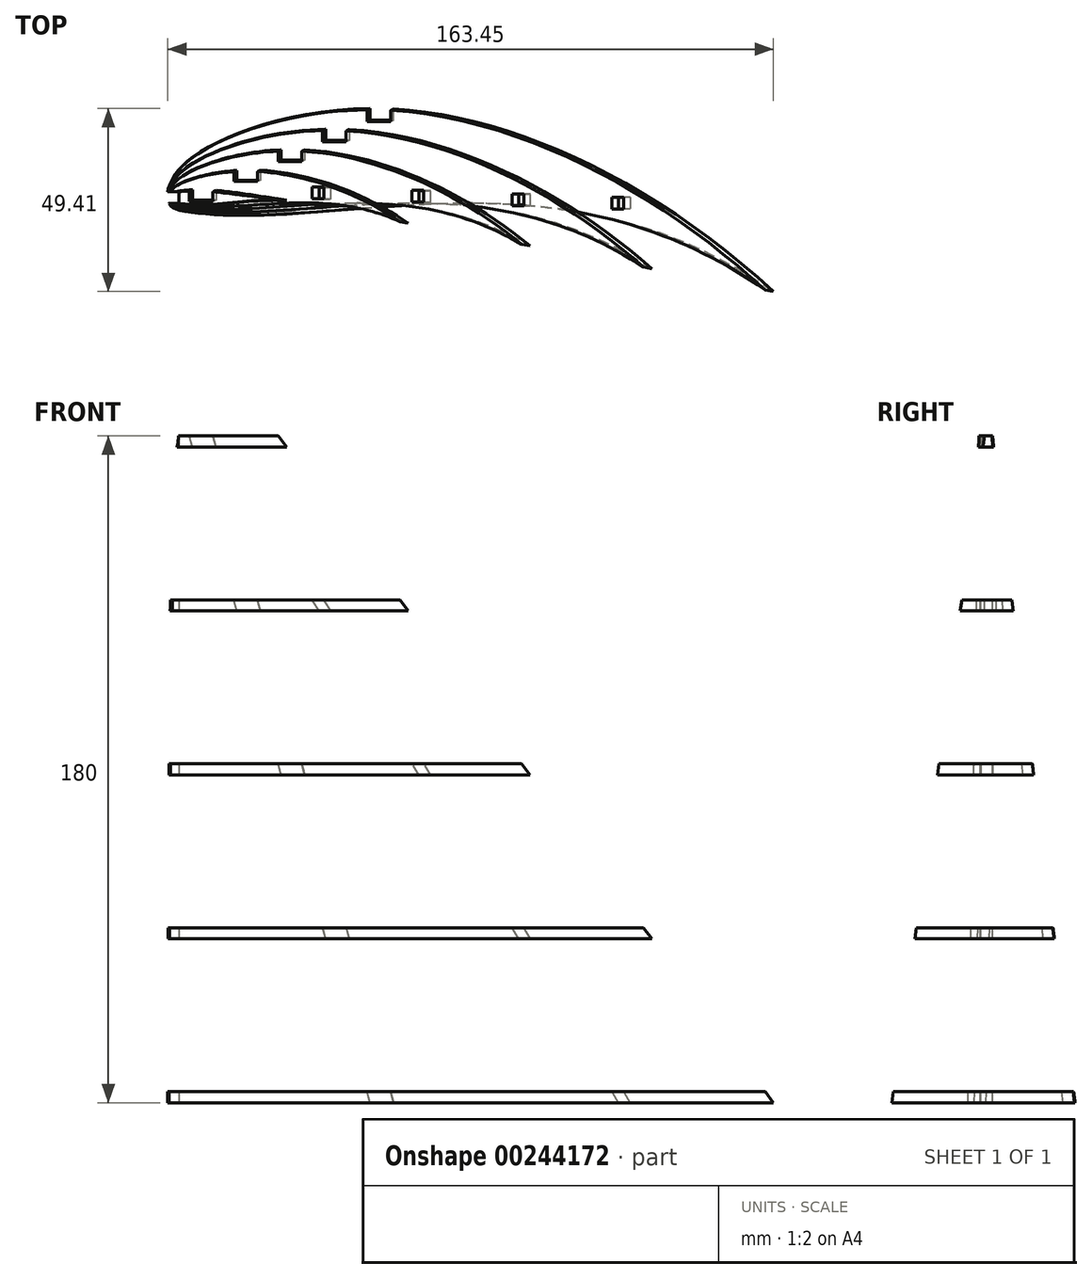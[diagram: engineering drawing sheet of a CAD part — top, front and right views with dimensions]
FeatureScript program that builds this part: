
annotation { "Feature Type Name" : "Feature", "Feature Type Description" : "" }
export const myFeature = defineFeature(function(context is Context, id is Id, definition is map)
    precondition{}
    {
        {
            var Q0;
            Q0=qCreatedBy(makeId("Top.planeOp"),FACE);
            var sketch = newSketch(context, id + "F0", { "sketchPlane" : qUnion([Q0])});
            skLineSegment(sketch, "E0", {"start": v(1.56, 5.68) * mm, "end": v(5.56, 9.57) * mm});
            skLineSegment(sketch, "E1", {"start": v(5.56, 9.57) * mm, "end": v(7.64, 11.4) * mm});
            skLineSegment(sketch, "E2", {"start": v(7.64, 11.4) * mm, "end": v(10.4, 13.54) * mm});
            skLineSegment(sketch, "E3", {"start": v(10.4, 13.54) * mm, "end": v(12.1, 14.65) * mm});
            skLineSegment(sketch, "E4", {"start": v(12.1, 14.65) * mm, "end": v(14.51, 16.01) * mm});
            skLineSegment(sketch, "E5", {"start": v(14.51, 16.01) * mm, "end": v(17.02, 17.22) * mm});
            skLineSegment(sketch, "E6", {"start": v(17.02, 17.22) * mm, "end": v(19.6, 18.28) * mm});
            skLineSegment(sketch, "E7", {"start": v(19.6, 18.28) * mm, "end": v(22.25, 19.22) * mm});
            skLineSegment(sketch, "E8", {"start": v(22.25, 19.22) * mm, "end": v(25.63, 20.25) * mm});
            skLineSegment(sketch, "E9", {"start": v(25.63, 20.25) * mm, "end": v(27.63, 20.8) * mm});
            skLineSegment(sketch, "E10", {"start": v(27.63, 20.8) * mm, "end": v(30.34, 21.45) * mm});
            skLineSegment(sketch, "E11", {"start": v(30.34, 21.45) * mm, "end": v(33.06, 22.02) * mm});
            skLineSegment(sketch, "E12", {"start": v(33.06, 22.02) * mm, "end": v(35.8, 22.52) * mm});
            skLineSegment(sketch, "E13", {"start": v(35.8, 22.52) * mm, "end": v(38.53, 22.94) * mm});
            skLineSegment(sketch, "E14", {"start": v(38.53, 22.94) * mm, "end": v(41.28, 23.3) * mm});
            skLineSegment(sketch, "E15", {"start": v(41.28, 23.3) * mm, "end": v(45.44, 23.69) * mm});
            skLineSegment(sketch, "E16", {"start": v(45.44, 23.69) * mm, "end": v(52.36, 24.01) * mm});
            skLineSegment(sketch, "E17", {"start": v(52.36, 24.01) * mm, "end": v(57.92, 23.98) * mm});
            skLineSegment(sketch, "E18", {"start": v(57.92, 23.98) * mm, "end": v(63.48, 23.67) * mm});
            skLineSegment(sketch, "E19", {"start": v(63.48, 23.67) * mm, "end": v(68.2, 23.2) * mm});
            skLineSegment(sketch, "E20", {"start": v(68.2, 23.2) * mm, "end": v(74.5, 22.25) * mm});
            skLineSegment(sketch, "E21", {"start": v(74.5, 22.25) * mm, "end": v(79.94, 21.16) * mm});
            skLineSegment(sketch, "E22", {"start": v(79.94, 21.16) * mm, "end": v(85.34, 19.84) * mm});
            skLineSegment(sketch, "E23", {"start": v(85.34, 19.84) * mm, "end": v(91.78, 17.96) * mm});
            skLineSegment(sketch, "E24", {"start": v(91.78, 17.96) * mm, "end": v(95.97, 16.57) * mm});
            skLineSegment(sketch, "E25", {"start": v(95.97, 16.57) * mm, "end": v(101.2, 14.66) * mm});
            skLineSegment(sketch, "E26", {"start": v(101.2, 14.66) * mm, "end": v(106.35, 12.57) * mm});
            skLineSegment(sketch, "E27", {"start": v(106.35, 12.57) * mm, "end": v(111.41, 10.3) * mm});
            skLineSegment(sketch, "E28", {"start": v(111.41, 10.3) * mm, "end": v(114.54, 8.79) * mm});
            skLineSegment(sketch, "E29", {"start": v(114.54, 8.79) * mm, "end": v(121.24, 5.25) * mm});
            skLineSegment(sketch, "E30", {"start": v(121.24, 5.25) * mm, "end": v(126.03, 2.48) * mm});
            skLineSegment(sketch, "E31", {"start": v(126.03, 2.48) * mm, "end": v(130.76, -0.45) * mm});
            skLineSegment(sketch, "E32", {"start": v(130.76, -0.45) * mm, "end": v(134.68, -3) * mm});
            skLineSegment(sketch, "E33", {"start": v(134.68, -3) * mm, "end": v(140.13, -6.74) * mm});
            skLineSegment(sketch, "E34", {"start": v(140.13, -6.74) * mm, "end": v(144.69, -10.02) * mm});
            skLineSegment(sketch, "E35", {"start": v(144.69, -10.02) * mm, "end": v(150.73, -14.63) * mm});
            skLineSegment(sketch, "E36", {"start": v(150.73, -14.63) * mm, "end": v(153.15, -16.57) * mm});
            skLineSegment(sketch, "E37", {"start": v(153.15, -16.57) * mm, "end": v(155.17, -18.23) * mm});
            skLineSegment(sketch, "E38", {"start": v(155.17, -18.23) * mm, "end": v(157.28, -19.98) * mm});
            skLineSegment(sketch, "E39", {"start": v(157.28, -19.98) * mm, "end": v(159.53, -21.87) * mm});
            skLineSegment(sketch, "E40", {"start": v(159.53, -21.87) * mm, "end": v(161.04, -23.14) * mm});
            skLineSegment(sketch, "E41", {"start": v(161.04, -23.14) * mm, "end": v(162.55, -24.41) * mm});
            skLineSegment(sketch, "E42", {"start": v(162.55, -24.41) * mm, "end": v(163.03, -24.83) * mm});
            skLineSegment(sketch, "E43", {"start": v(163.03, -24.83) * mm, "end": v(163.34, -25.1) * mm});
            skLineSegment(sketch, "E44", {"start": v(163.34, -25.1) * mm, "end": v(163.57, -25.34) * mm});
            skLineSegment(sketch, "E45", {"start": v(163.57, -25.34) * mm, "end": v(163.6, -25.41) * mm});
            skLineSegment(sketch, "E46", {"start": v(163.6, -25.41) * mm, "end": v(163.5, -25.38) * mm});
            skLineSegment(sketch, "E47", {"start": v(163.5, -25.38) * mm, "end": v(163.25, -25.24) * mm});
            skLineSegment(sketch, "E48", {"start": v(163.25, -25.24) * mm, "end": v(162.89, -25.02) * mm});
            skLineSegment(sketch, "E49", {"start": v(162.89, -25.02) * mm, "end": v(162.42, -24.7) * mm});
            skLineSegment(sketch, "E50", {"start": v(162.42, -24.7) * mm, "end": v(161.85, -24.33) * mm});
            skLineSegment(sketch, "E51", {"start": v(161.85, -24.33) * mm, "end": v(161.2, -23.89) * mm});
            skLineSegment(sketch, "E52", {"start": v(161.2, -23.89) * mm, "end": v(160.46, -23.39) * mm});
            skLineSegment(sketch, "E53", {"start": v(160.46, -23.39) * mm, "end": v(158.82, -22.27) * mm});
            skLineSegment(sketch, "E54", {"start": v(158.82, -22.27) * mm, "end": v(157.02, -21.04) * mm});
            skLineSegment(sketch, "E55", {"start": v(157.02, -21.04) * mm, "end": v(153.51, -18.72) * mm});
            skLineSegment(sketch, "E56", {"start": v(153.51, -18.72) * mm, "end": v(151.5, -17.45) * mm});
            skLineSegment(sketch, "E57", {"start": v(151.5, -17.45) * mm, "end": v(149.82, -16.42) * mm});
            skLineSegment(sketch, "E58", {"start": v(149.82, -16.42) * mm, "end": v(148.21, -15.5) * mm});
            skLineSegment(sketch, "E59", {"start": v(148.21, -15.5) * mm, "end": v(146.7, -14.65) * mm});
            skLineSegment(sketch, "E60", {"start": v(146.7, -14.65) * mm, "end": v(145.24, -13.9) * mm});
            skLineSegment(sketch, "E61", {"start": v(145.24, -13.9) * mm, "end": v(143.85, -13.2) * mm});
            skLineSegment(sketch, "E62", {"start": v(143.85, -13.2) * mm, "end": v(142.52, -12.6) * mm});
            skLineSegment(sketch, "E63", {"start": v(142.52, -12.6) * mm, "end": v(141.24, -12.04) * mm});
            skLineSegment(sketch, "E64", {"start": v(141.24, -12.04) * mm, "end": v(138.82, -11.11) * mm});
            skLineSegment(sketch, "E65", {"start": v(138.82, -11.11) * mm, "end": v(136.53, -10.36) * mm});
            skLineSegment(sketch, "E66", {"start": v(136.53, -10.36) * mm, "end": v(134.32, -9.76) * mm});
            skLineSegment(sketch, "E67", {"start": v(134.32, -9.76) * mm, "end": v(129.95, -8.78) * mm});
            skLineSegment(sketch, "E68", {"start": v(129.95, -8.78) * mm, "end": v(128.13, -8.4) * mm});
            skLineSegment(sketch, "E69", {"start": v(128.13, -8.4) * mm, "end": v(125.32, -7.82) * mm});
            skLineSegment(sketch, "E70", {"start": v(125.32, -7.82) * mm, "end": v(122.86, -7.3) * mm});
            skLineSegment(sketch, "E71", {"start": v(122.86, -7.3) * mm, "end": v(120.3, -6.74) * mm});
            skLineSegment(sketch, "E72", {"start": v(120.3, -6.74) * mm, "end": v(114.98, -5.62) * mm});
            skLineSegment(sketch, "E73", {"start": v(114.98, -5.62) * mm, "end": v(109.42, -4.5) * mm});
            skLineSegment(sketch, "E74", {"start": v(109.42, -4.5) * mm, "end": v(103.71, -3.46) * mm});
            skLineSegment(sketch, "E75", {"start": v(103.71, -3.46) * mm, "end": v(97.93, -2.53) * mm});
            skLineSegment(sketch, "E76", {"start": v(97.93, -2.53) * mm, "end": v(91.13, -1.7) * mm});
            skLineSegment(sketch, "E77", {"start": v(91.13, -1.7) * mm, "end": v(86.47, -1.3) * mm});
            skLineSegment(sketch, "E78", {"start": v(86.47, -1.3) * mm, "end": v(80.86, -1.04) * mm});
            skLineSegment(sketch, "E79", {"start": v(80.86, -1.04) * mm, "end": v(75.32, -0.97) * mm});
            skLineSegment(sketch, "E80", {"start": v(75.32, -0.97) * mm, "end": v(69.81, -1.08) * mm});
            skLineSegment(sketch, "E81", {"start": v(69.81, -1.08) * mm, "end": v(64.32, -1.32) * mm});
            skLineSegment(sketch, "E82", {"start": v(64.32, -1.32) * mm, "end": v(53.96, -2.02) * mm});
            skLineSegment(sketch, "E83", {"start": v(53.96, -2.02) * mm, "end": v(47.7, -2.53) * mm});
            skLineSegment(sketch, "E84", {"start": v(47.7, -2.53) * mm, "end": v(36.53, -3.57) * mm});
            skLineSegment(sketch, "E85", {"start": v(36.53, -3.57) * mm, "end": v(31.03, -4.15) * mm});
            skLineSegment(sketch, "E86", {"start": v(31.03, -4.15) * mm, "end": v(25.3, -4.8) * mm});
            skLineSegment(sketch, "E87", {"start": v(25.3, -4.8) * mm, "end": v(20.36, -5.36) * mm});
            skLineSegment(sketch, "E88", {"start": v(20.36, -5.36) * mm, "end": v(17.7, -5.56) * mm});
            skLineSegment(sketch, "E89", {"start": v(17.7, -5.56) * mm, "end": v(14.96, -5.63) * mm});
            skLineSegment(sketch, "E90", {"start": v(14.96, -5.63) * mm, "end": v(12.13, -5.52) * mm});
            skLineSegment(sketch, "E91", {"start": v(12.13, -5.52) * mm, "end": v(10.66, -5.39) * mm});
            skLineSegment(sketch, "E92", {"start": v(10.66, -5.39) * mm, "end": v(9.15, -5.2) * mm});
            skLineSegment(sketch, "E93", {"start": v(9.15, -5.2) * mm, "end": v(7.78, -4.97) * mm});
            skLineSegment(sketch, "E94", {"start": v(7.78, -4.97) * mm, "end": v(6.02, -4.6) * mm});
            skLineSegment(sketch, "E95", {"start": v(6.02, -4.6) * mm, "end": v(4.48, -4.16) * mm});
            skLineSegment(sketch, "E96", {"start": v(4.48, -4.16) * mm, "end": v(3.06, -3.62) * mm});
            skLineSegment(sketch, "E97", {"start": v(3.06, -3.62) * mm, "end": v(1.82, -2.95) * mm});
            skLineSegment(sketch, "E98", {"start": v(1.82, -2.95) * mm, "end": v(1.3, -2.56) * mm});
            skLineSegment(sketch, "E99", {"start": v(1.3, -2.56) * mm, "end": v(0.85, -2.13) * mm});
            skLineSegment(sketch, "E100", {"start": v(0.85, -2.13) * mm, "end": v(0.5, -1.66) * mm});
            skLineSegment(sketch, "E101", {"start": v(0.5, -1.66) * mm, "end": v(0.25, -1.2) * mm});
            skLineSegment(sketch, "E102", {"start": v(0.25, -1.2) * mm, "end": v(0.07, -0.6) * mm});
            skLineSegment(sketch, "E103", {"start": v(0.07, -0.6) * mm, "end": v(0, 0) * mm});
            skLineSegment(sketch, "E104", {"start": v(0, 0) * mm, "end": v(0.01, 0.63) * mm});
            skLineSegment(sketch, "E105", {"start": v(0.01, 0.63) * mm, "end": v(0.1, 1.3) * mm});
            skLineSegment(sketch, "E106", {"start": v(0.1, 1.3) * mm, "end": v(0.45, 2.7) * mm});
            skLineSegment(sketch, "E107", {"start": v(0.45, 2.7) * mm, "end": v(0.96, 4.17) * mm});
            skLineSegment(sketch, "E108", {"start": v(0.96, 4.17) * mm, "end": v(1.56, 5.68) * mm});
            skSolve(sketch);
        }
        {
            var Q0;
            Q0=qCreatedBy(makeId("Top.planeOp"),FACE);
            cPlane(context, id + "F1", {"entities" : qUnion([Q0]), "cplaneType" : CPlaneType.OFFSET, "offset" : 180 * mm, "width" : 150 * mm, "height" : 150 * mm});
        }
        {
            var Q0;
            Q0=qCreatedBy(id+"F1.planeOp",FACE);
            var sketch = newSketch(context, id + "F2", { "sketchPlane" : qUnion([Q0])});
            skLineSegment(sketch, "E109", {"start": v(0, 0) * mm, "end": v(0.3, 0.38) * mm});
            skLineSegment(sketch, "E110", {"start": v(0.3, 0.38) * mm, "end": v(0.47, 0.56) * mm});
            skLineSegment(sketch, "E111", {"start": v(0.47, 0.56) * mm, "end": v(0.63, 0.72) * mm});
            skLineSegment(sketch, "E112", {"start": v(0.63, 0.72) * mm, "end": v(0.8, 0.86) * mm});
            skLineSegment(sketch, "E113", {"start": v(0.8, 0.86) * mm, "end": v(1, 1) * mm});
            skLineSegment(sketch, "E114", {"start": v(1, 1) * mm, "end": v(1.22, 1.1) * mm});
            skLineSegment(sketch, "E115", {"start": v(1.22, 1.1) * mm, "end": v(1.43, 1.2) * mm});
            skLineSegment(sketch, "E116", {"start": v(1.43, 1.2) * mm, "end": v(1.66, 1.26) * mm});
            skLineSegment(sketch, "E117", {"start": v(1.66, 1.26) * mm, "end": v(1.9, 1.32) * mm});
            skLineSegment(sketch, "E118", {"start": v(1.9, 1.32) * mm, "end": v(2.38, 1.4) * mm});
            skLineSegment(sketch, "E119", {"start": v(2.38, 1.4) * mm, "end": v(3.07, 1.49) * mm});
            skLineSegment(sketch, "E120", {"start": v(3.07, 1.49) * mm, "end": v(4.34, 1.61) * mm});
            skLineSegment(sketch, "E121", {"start": v(4.34, 1.61) * mm, "end": v(5.28, 1.69) * mm});
            skLineSegment(sketch, "E122", {"start": v(5.28, 1.69) * mm, "end": v(6.67, 1.76) * mm});
            skLineSegment(sketch, "E123", {"start": v(6.67, 1.76) * mm, "end": v(7.17, 1.76) * mm});
            skLineSegment(sketch, "E124", {"start": v(7.17, 1.76) * mm, "end": v(8.12, 1.75) * mm});
            skLineSegment(sketch, "E125", {"start": v(8.12, 1.75) * mm, "end": v(9.07, 1.72) * mm});
            skLineSegment(sketch, "E126", {"start": v(9.07, 1.72) * mm, "end": v(10.03, 1.66) * mm});
            skLineSegment(sketch, "E127", {"start": v(10.03, 1.66) * mm, "end": v(11.22, 1.58) * mm});
            skLineSegment(sketch, "E128", {"start": v(11.22, 1.58) * mm, "end": v(12.9, 1.43) * mm});
            skLineSegment(sketch, "E129", {"start": v(12.9, 1.43) * mm, "end": v(14.8, 1.24) * mm});
            skLineSegment(sketch, "E130", {"start": v(14.8, 1.24) * mm, "end": v(16.34, 1.07) * mm});
            skLineSegment(sketch, "E131", {"start": v(16.34, 1.07) * mm, "end": v(18.57, 0.8) * mm});
            skLineSegment(sketch, "E132", {"start": v(18.57, 0.8) * mm, "end": v(20.47, 0.56) * mm});
            skLineSegment(sketch, "E133", {"start": v(20.47, 0.56) * mm, "end": v(21.43, 0.45) * mm});
            skLineSegment(sketch, "E134", {"start": v(21.43, 0.45) * mm, "end": v(22.43, 0.33) * mm});
            skLineSegment(sketch, "E135", {"start": v(22.43, 0.33) * mm, "end": v(23.42, 0.21) * mm});
            skLineSegment(sketch, "E136", {"start": v(23.42, 0.21) * mm, "end": v(24.38, 0.1) * mm});
            skLineSegment(sketch, "E137", {"start": v(24.38, 0.1) * mm, "end": v(24.84, 0.04) * mm});
            skLineSegment(sketch, "E138", {"start": v(24.84, 0.04) * mm, "end": v(25.3, -0.01) * mm});
            skLineSegment(sketch, "E139", {"start": v(25.3, -0.01) * mm, "end": v(25.9, -0.09) * mm});
            skLineSegment(sketch, "E140", {"start": v(25.9, -0.09) * mm, "end": v(26.15, -0.12) * mm});
            skLineSegment(sketch, "E141", {"start": v(26.15, -0.12) * mm, "end": v(26.97, -0.22) * mm});
            skLineSegment(sketch, "E142", {"start": v(26.97, -0.22) * mm, "end": v(27.4, -0.27) * mm});
            skLineSegment(sketch, "E143", {"start": v(27.4, -0.27) * mm, "end": v(27.65, -0.29) * mm});
            skLineSegment(sketch, "E144", {"start": v(27.65, -0.29) * mm, "end": v(27.9, -0.3) * mm});
            skLineSegment(sketch, "E145", {"start": v(27.9, -0.3) * mm, "end": v(28.16, -0.32) * mm});
            skLineSegment(sketch, "E146", {"start": v(28.16, -0.32) * mm, "end": v(28.45, -0.34) * mm});
            skLineSegment(sketch, "E147", {"start": v(28.45, -0.34) * mm, "end": v(28.76, -0.35) * mm});
            skLineSegment(sketch, "E148", {"start": v(28.76, -0.35) * mm, "end": v(28.93, -0.36) * mm});
            skLineSegment(sketch, "E149", {"start": v(28.93, -0.36) * mm, "end": v(29.42, -0.37) * mm});
            skLineSegment(sketch, "E150", {"start": v(29.42, -0.37) * mm, "end": v(29.57, -0.37) * mm});
            skLineSegment(sketch, "E151", {"start": v(29.57, -0.37) * mm, "end": v(29.71, -0.38) * mm});
            skLineSegment(sketch, "E152", {"start": v(29.71, -0.38) * mm, "end": v(29.83, -0.38) * mm});
            skLineSegment(sketch, "E153", {"start": v(29.83, -0.38) * mm, "end": v(29.92, -0.38) * mm});
            skLineSegment(sketch, "E154", {"start": v(29.92, -0.38) * mm, "end": v(29.98, -0.38) * mm});
            skLineSegment(sketch, "E155", {"start": v(29.98, -0.38) * mm, "end": v(30, -0.39) * mm});
            skLineSegment(sketch, "E156", {"start": v(30, -0.39) * mm, "end": v(29.98, -0.39) * mm});
            skLineSegment(sketch, "E157", {"start": v(29.98, -0.39) * mm, "end": v(29.92, -0.4) * mm});
            skLineSegment(sketch, "E158", {"start": v(29.92, -0.4) * mm, "end": v(29.83, -0.4) * mm});
            skLineSegment(sketch, "E159", {"start": v(29.83, -0.4) * mm, "end": v(29.72, -0.4) * mm});
            skLineSegment(sketch, "E160", {"start": v(29.72, -0.4) * mm, "end": v(29.58, -0.4) * mm});
            skLineSegment(sketch, "E161", {"start": v(29.58, -0.4) * mm, "end": v(29.42, -0.4) * mm});
            skLineSegment(sketch, "E162", {"start": v(29.42, -0.4) * mm, "end": v(28.93, -0.42) * mm});
            skLineSegment(sketch, "E163", {"start": v(28.93, -0.42) * mm, "end": v(28.76, -0.42) * mm});
            skLineSegment(sketch, "E164", {"start": v(28.76, -0.42) * mm, "end": v(28.45, -0.43) * mm});
            skLineSegment(sketch, "E165", {"start": v(28.45, -0.43) * mm, "end": v(28.17, -0.44) * mm});
            skLineSegment(sketch, "E166", {"start": v(28.17, -0.44) * mm, "end": v(27.9, -0.46) * mm});
            skLineSegment(sketch, "E167", {"start": v(27.9, -0.46) * mm, "end": v(27.65, -0.47) * mm});
            skLineSegment(sketch, "E168", {"start": v(27.65, -0.47) * mm, "end": v(27.4, -0.49) * mm});
            skLineSegment(sketch, "E169", {"start": v(27.4, -0.49) * mm, "end": v(26.96, -0.52) * mm});
            skLineSegment(sketch, "E170", {"start": v(26.96, -0.52) * mm, "end": v(26.14, -0.6) * mm});
            skLineSegment(sketch, "E171", {"start": v(26.14, -0.6) * mm, "end": v(25.86, -0.62) * mm});
            skLineSegment(sketch, "E172", {"start": v(25.86, -0.62) * mm, "end": v(25.3, -0.68) * mm});
            skLineSegment(sketch, "E173", {"start": v(25.3, -0.68) * mm, "end": v(24.84, -0.72) * mm});
            skLineSegment(sketch, "E174", {"start": v(24.84, -0.72) * mm, "end": v(24.37, -0.77) * mm});
            skLineSegment(sketch, "E175", {"start": v(24.37, -0.77) * mm, "end": v(23.4, -0.86) * mm});
            skLineSegment(sketch, "E176", {"start": v(23.4, -0.86) * mm, "end": v(22.42, -0.95) * mm});
            skLineSegment(sketch, "E177", {"start": v(22.42, -0.95) * mm, "end": v(21.43, -1.04) * mm});
            skLineSegment(sketch, "E178", {"start": v(21.43, -1.04) * mm, "end": v(20.45, -1.13) * mm});
            skLineSegment(sketch, "E179", {"start": v(20.45, -1.13) * mm, "end": v(18.55, -1.3) * mm});
            skLineSegment(sketch, "E180", {"start": v(18.55, -1.3) * mm, "end": v(16.28, -1.52) * mm});
            skLineSegment(sketch, "E181", {"start": v(16.28, -1.52) * mm, "end": v(12.87, -1.8) * mm});
            skLineSegment(sketch, "E182", {"start": v(12.87, -1.8) * mm, "end": v(11.19, -1.9) * mm});
            skLineSegment(sketch, "E183", {"start": v(11.19, -1.9) * mm, "end": v(10, -1.95) * mm});
            skLineSegment(sketch, "E184", {"start": v(10, -1.95) * mm, "end": v(9.03, -1.98) * mm});
            skLineSegment(sketch, "E185", {"start": v(9.03, -1.98) * mm, "end": v(8.08, -1.98) * mm});
            skLineSegment(sketch, "E186", {"start": v(8.08, -1.98) * mm, "end": v(7.13, -1.96) * mm});
            skLineSegment(sketch, "E187", {"start": v(7.13, -1.96) * mm, "end": v(6.6, -1.93) * mm});
            skLineSegment(sketch, "E188", {"start": v(6.6, -1.93) * mm, "end": v(5.24, -1.83) * mm});
            skLineSegment(sketch, "E189", {"start": v(5.24, -1.83) * mm, "end": v(4.3, -1.74) * mm});
            skLineSegment(sketch, "E190", {"start": v(4.3, -1.74) * mm, "end": v(3.04, -1.58) * mm});
            skLineSegment(sketch, "E191", {"start": v(3.04, -1.58) * mm, "end": v(2.35, -1.47) * mm});
            skLineSegment(sketch, "E192", {"start": v(2.35, -1.47) * mm, "end": v(1.87, -1.37) * mm});
            skLineSegment(sketch, "E193", {"start": v(1.87, -1.37) * mm, "end": v(1.64, -1.3) * mm});
            skLineSegment(sketch, "E194", {"start": v(1.64, -1.3) * mm, "end": v(1.41, -1.22) * mm});
            skLineSegment(sketch, "E195", {"start": v(1.41, -1.22) * mm, "end": v(1.2, -1.13) * mm});
            skLineSegment(sketch, "E196", {"start": v(1.2, -1.13) * mm, "end": v(1, -1.01) * mm});
            skLineSegment(sketch, "E197", {"start": v(1, -1.01) * mm, "end": v(0.77, -0.86) * mm});
            skLineSegment(sketch, "E198", {"start": v(0.77, -0.86) * mm, "end": v(0.62, -0.73) * mm});
            skLineSegment(sketch, "E199", {"start": v(0.62, -0.73) * mm, "end": v(0.46, -0.57) * mm});
            skLineSegment(sketch, "E200", {"start": v(0.46, -0.57) * mm, "end": v(0.3, -0.38) * mm});
            skLineSegment(sketch, "E201", {"start": v(0.3, -0.38) * mm, "end": v(0, 0) * mm});
            skSolve(sketch);
        }
        {
            var Q0;
            Q0=qCreatedBy(makeId("Top.planeOp"),FACE);
            var sketch = newSketch(context, id + "F3", { "sketchPlane" : qUnion([Q0])});
            skPoint(sketch, "E202.0", {"position": v(0, 0) * mm});
            skPoint(sketch, "E202.1", {"position": v(0.1, 1.3) * mm});
            skPoint(sketch, "E202.2", {"position": v(0.96, 4.17) * mm});
            skPoint(sketch, "E202.3", {"position": v(7.64, 11.4) * mm});
            skPoint(sketch, "E202.4", {"position": v(57.92, 23.98) * mm});
            skPoint(sketch, "E202.5", {"position": v(163.6, -25.41) * mm});
            skPoint(sketch, "E202.6", {"position": v(91.13, -1.7) * mm});
            skPoint(sketch, "E202.7", {"position": v(25.3, -4.8) * mm});
            skPoint(sketch, "E202.8", {"position": v(0.5, -1.66) * mm});
            skPoint(sketch, "E202.9", {"position": v(1.82, -2.95) * mm});
            skFitSpline(sketch, "E203", {"points": [v(0, 0) * mm, v(0.1, 1.3) * mm, v(0.96, 4.17) * mm, v(7.64, 11.4) * mm, v(57.92, 23.98) * mm, v(163.6, -25.41) * mm], "startDerivative": vector(0.92, 25.14) * mm, "endDerivative": vector(224.8, -205.78) * mm});
            skFitSpline(sketch, "E204", {"points": [v(0, 0) * mm, v(0.5, -1.66) * mm, v(1.82, -2.95) * mm, v(25.3, -4.8) * mm, v(91.13, -1.7) * mm, v(163.6, -25.41) * mm], "startDerivative": vector(7.8, -32.55) * mm, "endDerivative": vector(193.23, -135.32) * mm});
            skSolve(sketch);
        }
        {
            var Q0;
            Q0=qCreatedBy(id+"F1.planeOp",FACE);
            var sketch = newSketch(context, id + "F4", { "sketchPlane" : qUnion([Q0])});
            skPoint(sketch, "E205.0", {"position": v(0, 0) * mm});
            skPoint(sketch, "E205.1", {"position": v(0.8, 0.86) * mm});
            skPoint(sketch, "E205.2", {"position": v(1.66, 1.26) * mm});
            skPoint(sketch, "E205.3", {"position": v(8.12, 1.75) * mm});
            skPoint(sketch, "E205.4", {"position": v(21.43, 0.45) * mm});
            skPoint(sketch, "E205.5", {"position": v(30, -0.39) * mm});
            skPoint(sketch, "E205.6", {"position": v(21.43, -1.04) * mm});
            skPoint(sketch, "E205.7", {"position": v(8.08, -1.98) * mm});
            skPoint(sketch, "E205.8", {"position": v(0.77, -0.86) * mm});
            skPoint(sketch, "E205.9", {"position": v(1.64, -1.3) * mm});
            skFitSpline(sketch, "E206", {"points": [v(0, 0) * mm, v(0.8, 0.86) * mm, v(1.66, 1.26) * mm, v(8.12, 1.75) * mm, v(21.43, 0.45) * mm, v(30, -0.39) * mm], "startDerivative": vector(8.48, 10.03) * mm, "endDerivative": vector(30.3, -2.54) * mm});
            skFitSpline(sketch, "E207", {"points": [v(0, 0) * mm, v(0.77, -0.86) * mm, v(1.64, -1.3) * mm, v(8.08, -1.98) * mm, v(21.43, -1.04) * mm, v(30, -0.39) * mm], "startDerivative": vector(8.19, -10.03) * mm, "endDerivative": vector(30.3, 1.99) * mm});
            skSolve(sketch);
        }
        {
            var Q0;
            Q0=makeQuery(id+"F3.imprint","IMPRINT",FACE,{"disambiguationData":[TD([[makeQuery(id+"F3.imprint","IMPRINT",EDGE,{"derivedFrom":sQuery(id+"F3.wireOp",EDGE,"E203")}),-1.0]])]});
            var Q1;
            Q1=makeQuery(id+"F4.imprint","IMPRINT",FACE,{"disambiguationData":[TD([[makeQuery(id+"F4.imprint","IMPRINT",EDGE,{"derivedFrom":sQuery(id+"F4.wireOp",EDGE,"E206")}),-1.0]])]});
            loft(context, id + "F5", {"sheetProfilesArray" : [{ "sheetProfileEntities" : qUnion([Q0]) }, { "sheetProfileEntities" : qUnion([Q1]) }]});
        }
        {
            var Q0;
            Q0=qCreatedBy(makeId("Front.planeOp"),FACE);
            var sketch = newSketch(context, id + "F6", { "sketchPlane" : qUnion([Q0])});
            skLineSegment(sketch, "E208", {"start": v(0, 0) * mm, "end": v(0, 3) * mm, "construction": true});
            skLineSegment(sketch, "E209.bottom", {"start": v(0, 3) * mm, "end": v(207.09, 3) * mm});
            skLineSegment(sketch, "E209.top", {"start": v(0, 44.25) * mm, "end": v(207.09, 44.25) * mm});
            skLineSegment(sketch, "E209.left", {"start": v(0, 3) * mm, "end": v(0, 44.25) * mm});
            skLineSegment(sketch, "E209.right", {"start": v(207.09, 3) * mm, "end": v(207.09, 44.25) * mm});
            skLineSegment(sketch, "E210.0.1.0", {"start": v(0, 47.25) * mm, "end": v(207.09, 47.25) * mm});
            skLineSegment(sketch, "E210.0.1.1", {"start": v(0, 88.5) * mm, "end": v(207.09, 88.5) * mm});
            skLineSegment(sketch, "E210.0.1.2", {"start": v(0, 47.25) * mm, "end": v(0, 88.5) * mm});
            skLineSegment(sketch, "E210.0.1.3", {"start": v(207.09, 47.25) * mm, "end": v(207.09, 88.5) * mm});
            skLineSegment(sketch, "E210.0.1.4", {"start": v(0, 44.25) * mm, "end": v(0, 47.25) * mm, "construction": true});
            skLineSegment(sketch, "E210.0.2.0", {"start": v(0, 91.5) * mm, "end": v(207.09, 91.5) * mm});
            skLineSegment(sketch, "E210.0.2.1", {"start": v(0, 132.75) * mm, "end": v(207.09, 132.75) * mm});
            skLineSegment(sketch, "E210.0.2.2", {"start": v(0, 91.5) * mm, "end": v(0, 132.75) * mm});
            skLineSegment(sketch, "E210.0.2.3", {"start": v(207.09, 91.5) * mm, "end": v(207.09, 132.75) * mm});
            skLineSegment(sketch, "E210.0.2.4", {"start": v(0, 88.5) * mm, "end": v(0, 91.5) * mm, "construction": true});
            skLineSegment(sketch, "E210.0.3.0", {"start": v(0, 135.75) * mm, "end": v(207.09, 135.75) * mm});
            skLineSegment(sketch, "E210.0.3.1", {"start": v(0, 177) * mm, "end": v(207.09, 177) * mm});
            skLineSegment(sketch, "E210.0.3.2", {"start": v(0, 135.75) * mm, "end": v(0, 177) * mm});
            skLineSegment(sketch, "E210.0.3.3", {"start": v(207.09, 135.75) * mm, "end": v(207.09, 177) * mm});
            skLineSegment(sketch, "E210.0.3.4", {"start": v(0, 132.75) * mm, "end": v(0, 135.75) * mm, "construction": true});
            skLineSegment(sketch, "E210.direction1", {"start": v(0, 0) * mm, "end": v(25, 0) * mm, "construction": true});
            skLineSegment(sketch, "E210.direction2", {"start": v(0, 0) * mm, "end": v(0, 44.25) * mm, "construction": true});
            skSolve(sketch);
        }
        {
            var Q0;
            Q0 = qSketchRegion(id + "F6", true);
            extrude(context, id + "F7", {"entities" : qUnion([Q0]), "operationType" : NewBodyOperationType.REMOVE, "oppositeDirection" : true, "depth" : 50 * mm, "offsetDistance" : 25 * mm, "hasSecondDirection" : true, "secondDirectionOppositeDirection" : false, "secondDirectionDepth" : 50 * mm});
        }
        {
            var Q0;
            Q0=qCreatedBy(makeId("Top.planeOp"),FACE);
            var sketch = newSketch(context, id + "F8", { "sketchPlane" : qUnion([Q0])});
            skLineSegment(sketch, "E211", {"start": v(0, 0) * mm, "end": v(3.18, 0) * mm, "construction": true});
            skLineSegment(sketch, "E212", {"start": v(3.18, 0) * mm, "end": v(3.18, 1.59) * mm});
            skLineSegment(sketch, "E213", {"start": v(3.18, 0) * mm, "end": v(3.18, -1.59) * mm});
            skLineSegment(sketch, "E214", {"start": v(3.18, -1.59) * mm, "end": v(0, -1.59) * mm});
            skLineSegment(sketch, "E215", {"start": v(0, -1.59) * mm, "end": v(0, 1.59) * mm});
            skLineSegment(sketch, "E216", {"start": v(0, 1.59) * mm, "end": v(3.18, 1.59) * mm});
            skSolve(sketch);
        }
        {
            var Q0;
            Q0 = qSketchRegion(id + "F8", true);
            extrude(context, id + "F9", {"entities" : qUnion([Q0]), "operationType" : NewBodyOperationType.REMOVE, "depth" : 200 * mm, "offsetDistance" : 25 * mm});
        }
        {
            var Q0;
            Q0=makeQuery(id+"F3.imprint","IMPRINT",FACE,{"disambiguationData":[TD([[makeQuery(id+"F3.imprint","IMPRINT",EDGE,{"derivedFrom":sQuery(id+"F3.wireOp",EDGE,"E203")}),-1.0]])]});
            var sketch = newSketch(context, id + "F10", { "sketchPlane" : qUnion([Q0])});
            skPoint(sketch, "E217.0", {"position": v(57.92, 23.98) * mm});
            skLineSegment(sketch, "E218", {"start": v(57.92, 23.98) * mm, "end": v(57.92, 20.8) * mm, "construction": true});
            skLineSegment(sketch, "E219", {"start": v(57.92, 20.8) * mm, "end": v(54.75, 20.8) * mm});
            skLineSegment(sketch, "E220", {"start": v(57.92, 20.8) * mm, "end": v(61.1, 20.8) * mm});
            skLineSegment(sketch, "E221", {"start": v(61.1, 20.8) * mm, "end": v(61.1, 23.98) * mm});
            skLineSegment(sketch, "E222", {"start": v(61.1, 23.98) * mm, "end": v(54.75, 23.98) * mm, "construction": true});
            skLineSegment(sketch, "E223", {"start": v(54.75, 23.98) * mm, "end": v(54.75, 20.8) * mm});
            skLineSegment(sketch, "E224", {"start": v(61.1, 23.98) * mm, "end": v(61.1, 25.42) * mm});
            skLineSegment(sketch, "E225", {"start": v(61.1, 25.42) * mm, "end": v(54.75, 25.42) * mm});
            skLineSegment(sketch, "E226", {"start": v(54.75, 25.42) * mm, "end": v(54.75, 23.98) * mm});
            skSolve(sketch);
        }
        {
            var Q0;
            Q0=makeQuery(id+"F5.opLoft","CAP_FACE",FACE,{"disambiguationData":[OSD([makeQuery(id+"F4.imprint","IMPRINT",FACE,{"disambiguationData":[TD([[makeQuery(id+"F4.imprint","IMPRINT",EDGE,{"derivedFrom":sQuery(id+"F4.wireOp",EDGE,"E206")}),-1.0]])]})])],"isStart":true});
            var sketch = newSketch(context, id + "F11", { "sketchPlane" : qUnion([Q0])});
            skFitSpline(sketch, "E227.0", {"points": [v(32.22, -0.8) * mm, v(31, -0.59) * mm, v(28.55, -0.18) * mm, v(25.48, 0.28) * mm, v(23.02, 0.64) * mm, v(20.56, 1) * mm, v(17.48, 1.42) * mm, v(14.4, 1.77) * mm, v(11.92, 1.96) * mm, v(10.06, 2.06) * mm, v(8.2, 2.08) * mm, v(6.33, 2.02) * mm, v(4.47, 1.87) * mm, v(3.24, 1.7) * mm, v(2.63, 1.59) * mm], "construction": true});
            skLineSegment(sketch, "E228", {"start": v(9.16, 2.07) * mm, "end": v(9.16, -1.1) * mm, "construction": true});
            skLineSegment(sketch, "E229", {"start": v(9.16, -1.1) * mm, "end": v(12.33, -1.1) * mm});
            skLineSegment(sketch, "E230", {"start": v(9.16, -1.1) * mm, "end": v(5.98, -1.1) * mm});
            skLineSegment(sketch, "E231", {"start": v(12.33, -1.1) * mm, "end": v(12.33, 2.07) * mm});
            skLineSegment(sketch, "E232", {"start": v(12.33, 2.07) * mm, "end": v(5.98, 2.07) * mm});
            skLineSegment(sketch, "E233", {"start": v(5.98, 2.07) * mm, "end": v(5.98, -1.1) * mm});
            skSolve(sketch);
        }
        {
            var Q0;
            Q0=sQuery(id+"F10.wireOp",VERTEX,"E223.end");
            var Q1;
            Q1=sQuery(id+"F10.wireOp",VERTEX,"E226.start");
            var Q2;
            Q2=sQuery(id+"F11.wireOp",VERTEX,"E233.end");
            cPlane(context, id + "F12", {"entities" : qUnion([Q0, Q1, Q2]), "cplaneType" : CPlaneType.THREE_POINT, "offset" : 25 * mm, "width" : 150 * mm, "height" : 150 * mm});
        }
        {
            var Q0;
            Q0=qCreatedBy(id+"F12.planeOp",FACE);
            var sketch = newSketch(context, id + "F13", { "sketchPlane" : qUnion([Q0])});
            skPoint(sketch, "E234.0", {"position": v(-20.8, -14.32) * mm});
            skPoint(sketch, "E234.1", {"position": v(1.1, 172.17) * mm});
            skLineSegment(sketch, "E235", {"start": v(1.1, 172.17) * mm, "end": v(-20.8, -14.32) * mm});
            skSolve(sketch);
        }
        {
            var Q0;
            Q0 = qSketchRegion(id + "F10", true);
            var Q1;
            Q1=sQuery(id+"F13.wireOp",EDGE,"E235");
            sweep(context, id + "F14", {"operationType" : NewBodyOperationType.REMOVE, "profiles" : qUnion([Q0]), "path" : qUnion([Q1])});
        }
        {
            var Q0;
            Q0=makeQuery(id+"F3.imprint","IMPRINT",FACE,{"disambiguationData":[TD([[makeQuery(id+"F3.imprint","IMPRINT",EDGE,{"derivedFrom":sQuery(id+"F3.wireOp",EDGE,"E203")}),-1.0]])]});
            var sketch = newSketch(context, id + "F15", { "sketchPlane" : qUnion([Q0])});
            skLineSegment(sketch, "E236.bottom", {"start": v(125, 0) * mm, "end": v(121.82, 0) * mm});
            skLineSegment(sketch, "E236.top", {"start": v(125, -3.17) * mm, "end": v(121.82, -3.17) * mm});
            skLineSegment(sketch, "E236.left", {"start": v(125, 0) * mm, "end": v(125, -3.17) * mm});
            skLineSegment(sketch, "E236.right", {"start": v(121.82, 0) * mm, "end": v(121.82, -3.17) * mm});
            skSolve(sketch);
        }
        {
            var Q0;
            Q0=makeQuery(id+"F7.boolean.opBoolean","COPY",FACE,{"derivedFrom":makeQuery(id+"F7.opExtrude","SWEPT_FACE",FACE,{"disambiguationData":[OSD([sQuery(id+"F6.wireOp",EDGE,"E210.0.3.0")])]})});
            var sketch = newSketch(context, id + "F16", { "sketchPlane" : qUnion([Q0])});
            skLineSegment(sketch, "E237.bottom", {"start": v(39.15, 2.77) * mm, "end": v(42.32, 2.77) * mm});
            skLineSegment(sketch, "E237.top", {"start": v(39.15, -0.4) * mm, "end": v(42.32, -0.4) * mm});
            skLineSegment(sketch, "E237.left", {"start": v(39.15, 2.77) * mm, "end": v(39.15, -0.4) * mm});
            skLineSegment(sketch, "E237.right", {"start": v(42.32, 2.77) * mm, "end": v(42.32, -0.4) * mm});
            skSolve(sketch);
        }
        {
            var Q0;
            Q0 = qSketchRegion(id + "F15", true);
            var Q1;
            Q1 = qSketchRegion(id + "F16", true);
            loft(context, id + "F17", {"operationType" : NewBodyOperationType.REMOVE, "sheetProfilesArray" : [{ "sheetProfileEntities" : qUnion([Q0]) }, { "sheetProfileEntities" : qUnion([Q1]) }]});
        }
    });
